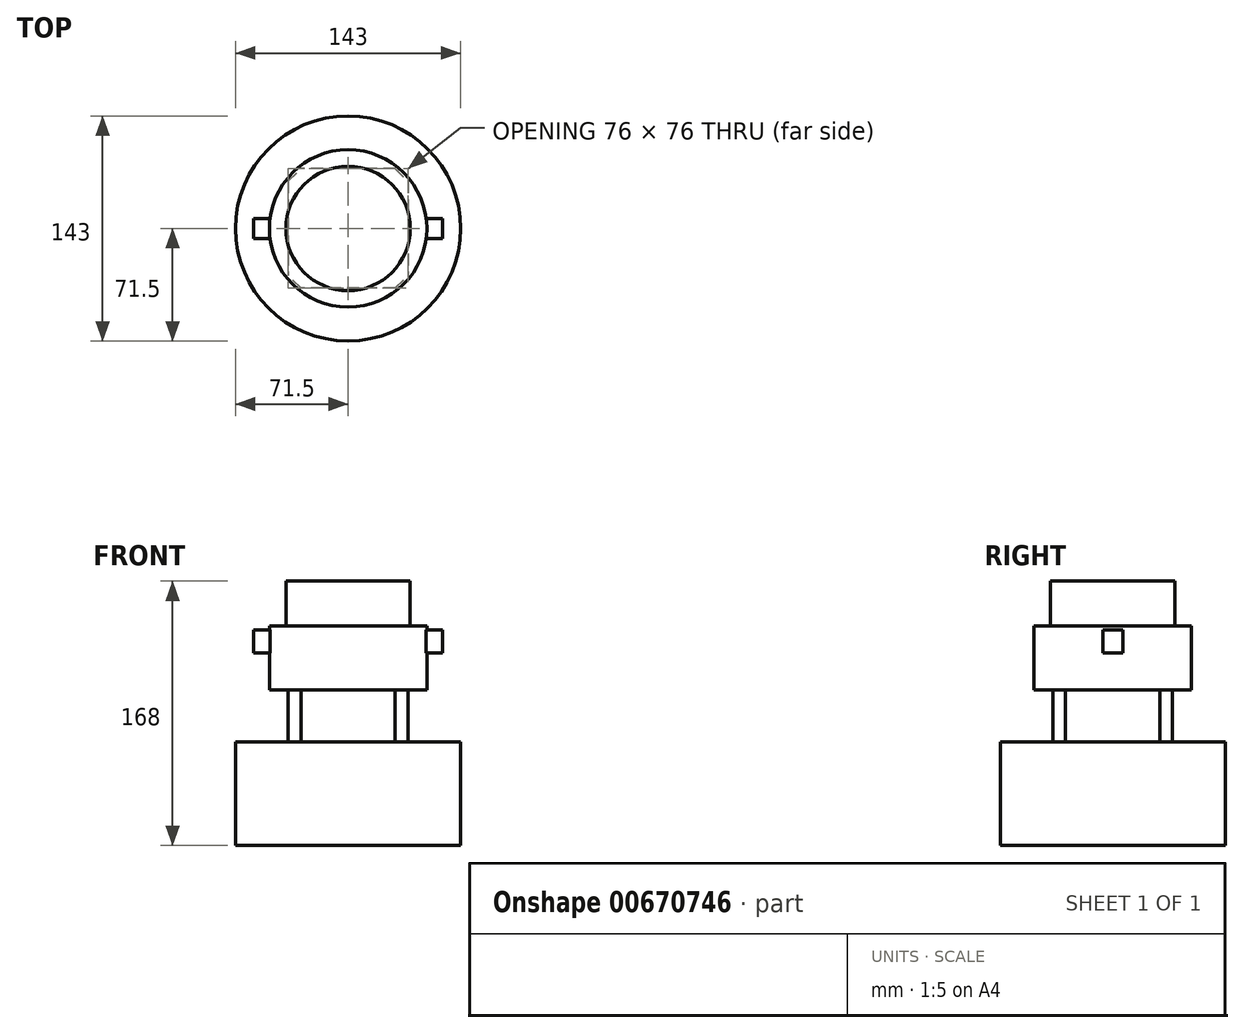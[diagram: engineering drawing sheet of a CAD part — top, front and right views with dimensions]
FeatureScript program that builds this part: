
annotation { "Feature Type Name" : "Feature", "Feature Type Description" : "" }
export const myFeature = defineFeature(function(context is Context, id is Id, definition is map)
    precondition{}
    {
        {
            var Q0;
            Q0=qCreatedBy(makeId("Front.planeOp"),FACE);
            var sketch = newSketch(context, id + "F0", { "sketchPlane" : qUnion([Q0])});
            skPoint(sketch, "E0.end.orphan", {"position": v(0, 66) * mm});
            skLineSegment(sketch, "E1.bottom", {"start": v(0, 0) * mm, "end": v(71.5, 0) * mm});
            skLineSegment(sketch, "E1.top", {"start": v(0, 66) * mm, "end": v(71.5, 66) * mm});
            skLineSegment(sketch, "E1.left", {"start": v(0, 0) * mm, "end": v(0, 66) * mm});
            skLineSegment(sketch, "E1.right", {"start": v(71.5, 0) * mm, "end": v(71.5, 66) * mm});
            skSolve(sketch);
        }
        {
            var Q0;
            Q0=makeQuery(id+"F0.imprint","IMPRINT",FACE,{"disambiguationData":[TD([[makeQuery(id+"F0.imprint","IMPRINT",EDGE,{"derivedFrom":sQuery(id+"F0.wireOp",EDGE,"E1.bottom")}),1.0]])]});
            var Q1;
            Q1=sQuery(id+"F0.wireOp",EDGE,"E1.left");
            revolve(context, id + "F1", {"entities" : qUnion([Q0]), "axis" : qUnion([Q1]), "revolveType" : RevolveType.FULL});
        }
        {
            var Q0;
            Q0=makeQuery(id+"F1.opRevolve","SWEPT_FACE",FACE,{"disambiguationData":[OSD([sQuery(id+"F0.wireOp",EDGE,"E1.top")])]});
            var sketch = newSketch(context, id + "F2", { "sketchPlane" : qUnion([Q0])});
            skLineSegment(sketch, "E2.bottom", {"start": v(30, 38) * mm, "end": v(-30, 38) * mm});
            skLineSegment(sketch, "E2.top", {"start": v(30, -38) * mm, "end": v(-30, -38) * mm});
            skLineSegment(sketch, "E2.left", {"start": v(38, 30) * mm, "end": v(38, -30) * mm});
            skLineSegment(sketch, "E2.right", {"start": v(-38, 30) * mm, "end": v(-38, -30) * mm});
            skPoint(sketch, "E2.middle", {"position": v(0, 0) * mm});
            skLineSegment(sketch, "E3", {"start": v(-38, 30) * mm, "end": v(-30, 38) * mm});
            skLineSegment(sketch, "E4", {"start": v(30, 38) * mm, "end": v(38, 30) * mm});
            skLineSegment(sketch, "E5", {"start": v(-30, -38) * mm, "end": v(-38, -30) * mm});
            skLineSegment(sketch, "E6", {"start": v(30, -38) * mm, "end": v(38, -30) * mm});
            skPoint(sketch, "E7.orphan", {"position": v(-38, 38) * mm});
            skPoint(sketch, "E8.orphan", {"position": v(38, 38) * mm});
            skPoint(sketch, "E9.orphan", {"position": v(38, -38) * mm});
            skPoint(sketch, "E10.orphan", {"position": v(-38, -38) * mm});
            skLineSegment(sketch, "E11", {"start": v(0, 0) * mm, "end": v(-38, 0) * mm, "construction": true});
            skSolve(sketch);
        }
        {
            var Q0;
            Q0=makeQuery(id+"F2.imprint","IMPRINT",FACE,{"disambiguationData":[TD([[makeQuery(id+"F2.imprint","IMPRINT",EDGE,{"derivedFrom":sQuery(id+"F2.wireOp",EDGE,"E2.bottom")}),1.0]])]});
            extrude(context, id + "F3", {"entities" : qUnion([Q0]), "operationType" : NewBodyOperationType.ADD, "depth" : 33 * mm, "offsetDistance" : 25 * mm});
        }
        {
            var Q0;
            Q0=makeQuery(id+"F3.opExtrude","CAP_FACE",FACE,{"disambiguationData":[OSD([sQuery(id+"F2.wireOp",EDGE,"E2.bottom"),sQuery(id+"F2.wireOp",EDGE,"E2.top"),sQuery(id+"F2.wireOp",EDGE,"E2.left"),sQuery(id+"F2.wireOp",EDGE,"E2.right")])],"isStart":false});
            var sketch = newSketch(context, id + "F4", { "sketchPlane" : qUnion([Q0])});
            skCircle(sketch, "E12", {"center": v(0, 0) * mm, "radius": 50 * mm});
            skSolve(sketch);
        }
        {
            var Q0;
            Q0=makeQuery(id+"F4.imprint","IMPRINT",FACE,{"disambiguationData":[TD([[makeQuery(id+"F4.imprint","IMPRINT",EDGE,{"derivedFrom":sQuery(id+"F4.wireOp",EDGE,"E12")}),1.0]])]});
            var Q1;
            Q1=makeQuery(id+"F4.imprint","IMPRINT",FACE,{"disambiguationData":[TD([[makeQuery(id+"F4.imprint","IMPRINT",EDGE,{"derivedFrom":makeQuery(id+"F3.opExtrude","CAP_EDGE",EDGE,{"disambiguationData":[OSD([sQuery(id+"F2.wireOp",EDGE,"E2.bottom")])],"isStart":false})}),1.0]])]});
            extrude(context, id + "F5", {"entities" : qUnion([Q0, Q1]), "operationType" : NewBodyOperationType.ADD, "depth" : 40.5 * mm, "offsetDistance" : 25 * mm});
        }
        {
            var Q0;
            Q0=makeQuery(id+"F5.opExtrude","CAP_FACE",FACE,{"disambiguationData":[OSD([sQuery(id+"F4.wireOp",EDGE,"E12")])],"isStart":false});
            var sketch = newSketch(context, id + "F6", { "sketchPlane" : qUnion([Q0])});
            skCircle(sketch, "E13", {"center": v(0, 0) * mm, "radius": 39.5 * mm});
            skSolve(sketch);
        }
        {
            var Q0;
            Q0=makeQuery(id+"F6.imprint","IMPRINT",FACE,{"disambiguationData":[TD([[makeQuery(id+"F6.imprint","IMPRINT",EDGE,{"derivedFrom":sQuery(id+"F6.wireOp",EDGE,"E13")}),1.0]])]});
            extrude(context, id + "F7", {"entities" : qUnion([Q0]), "operationType" : NewBodyOperationType.ADD, "depth" : 28.5 * mm, "offsetDistance" : 25 * mm});
        }
        {
            var Q0;
            Q0=qCreatedBy(makeId("Right.planeOp"),FACE);
            var sketch = newSketch(context, id + "F8", { "sketchPlane" : qUnion([Q0])});
            skLineSegment(sketch, "E14.bottom", {"start": v(-6.4, 137) * mm, "end": v(6.4, 137) * mm});
            skLineSegment(sketch, "E14.top", {"start": v(-6.4, 122.5) * mm, "end": v(6.4, 122.5) * mm});
            skLineSegment(sketch, "E14.left", {"start": v(-6.4, 137) * mm, "end": v(-6.4, 122.5) * mm});
            skLineSegment(sketch, "E14.right", {"start": v(6.4, 137) * mm, "end": v(6.4, 122.5) * mm});
            skLineSegment(sketch, "E15", {"start": v(0, 122.5) * mm, "end": v(0, 137) * mm, "construction": true});
            skSolve(sketch);
        }
        {
            var Q0;
            Q0 = qSketchRegion(id + "F8", true);
            var Q1;
            Q1=makeQuery(id+"F5.opExtrude","SWEPT_FACE",FACE,{"disambiguationData":[OSD([sQuery(id+"F4.wireOp",EDGE,"E12")])]});
            extrude(context, id + "F9", {"entities" : qUnion([Q0]), "operationType" : NewBodyOperationType.ADD, "endBound" : BoundingType.SYMMETRIC, "depth" : 120 * mm, "endBoundEntityFace" : qUnion([Q1]), "offsetDistance" : 25 * mm, "hasSecondDirection" : true, "secondDirectionOppositeDirection" : true, "secondDirectionDepth" : 25 * mm});
        }
    });
